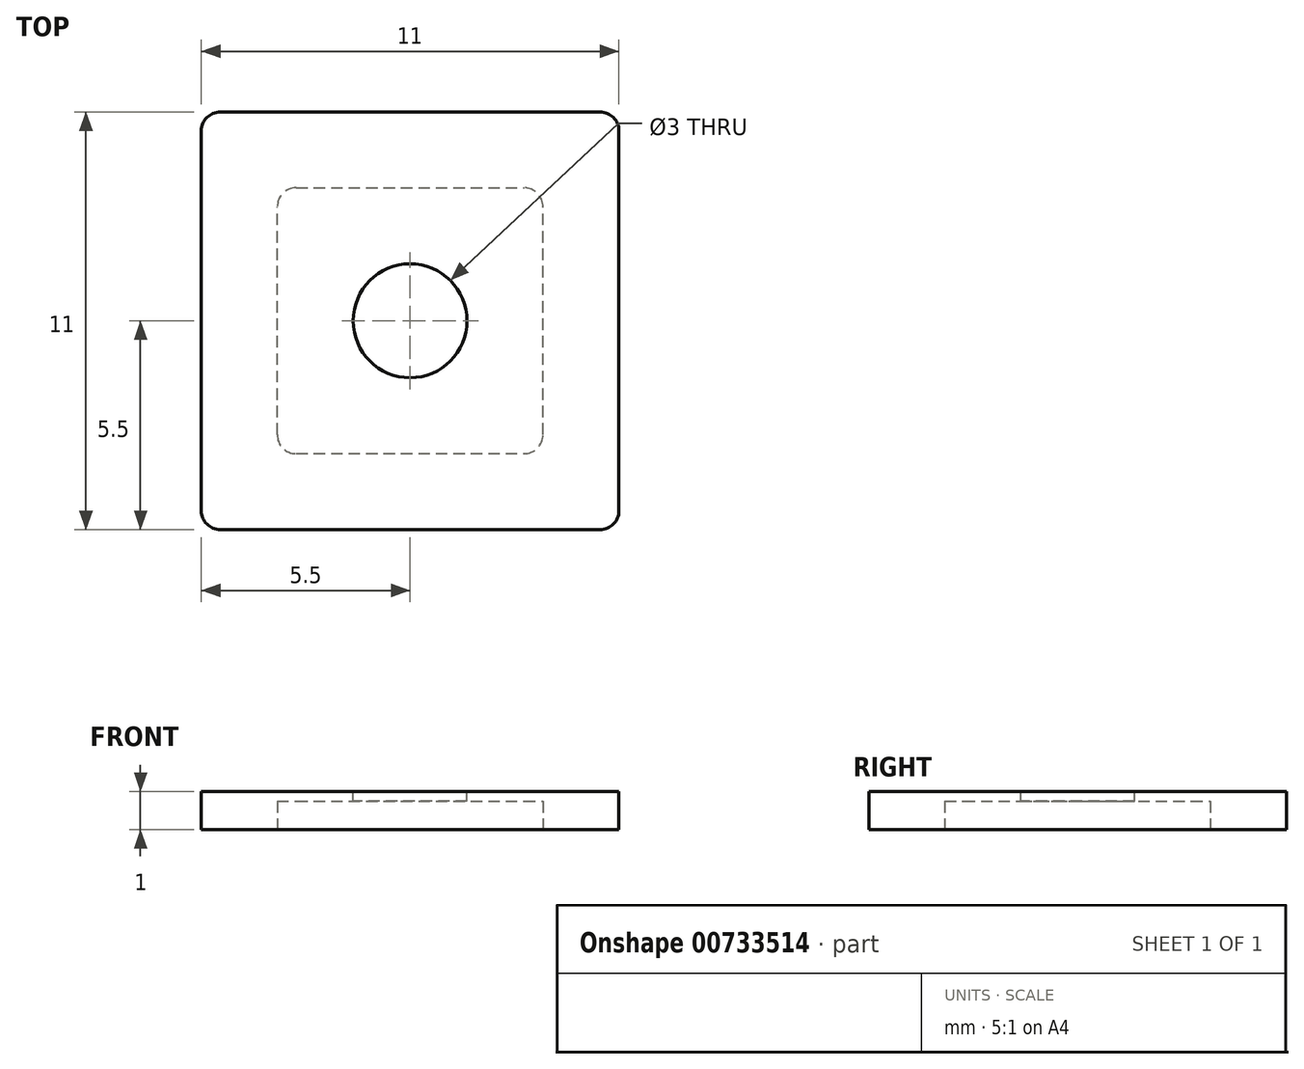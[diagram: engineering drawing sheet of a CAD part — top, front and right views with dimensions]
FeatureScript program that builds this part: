
annotation { "Feature Type Name" : "Feature", "Feature Type Description" : "" }
export const myFeature = defineFeature(function(context is Context, id is Id, definition is map)
    precondition{}
    {
        {
            var Q0;
            Q0=qCreatedBy(makeId("Top.planeOp"),FACE);
            var sketch = newSketch(context, id + "F0", { "sketchPlane" : qUnion([Q0])});
            skLineSegment(sketch, "E0.bottom", {"start": v(0, 0) * mm, "end": v(7, 0) * mm});
            skLineSegment(sketch, "E0.top", {"start": v(0, 7) * mm, "end": v(7, 7) * mm});
            skLineSegment(sketch, "E0.left", {"start": v(0, 0) * mm, "end": v(0, 7) * mm});
            skLineSegment(sketch, "E0.right", {"start": v(7, 0) * mm, "end": v(7, 7) * mm});
            skLineSegment(sketch, "E1.0", {"start": v(-2, 9) * mm, "end": v(9, 9) * mm});
            skLineSegment(sketch, "E1.1", {"start": v(-2, -2) * mm, "end": v(-2, 9) * mm});
            skLineSegment(sketch, "E1.2", {"start": v(-2, -2) * mm, "end": v(9, -2) * mm});
            skLineSegment(sketch, "E1.3", {"start": v(9, -2) * mm, "end": v(9, 9) * mm});
            skSolve(sketch);
        }
        {
            var Q0;
            Q0=makeQuery(id+"F0.imprint","IMPRINT",FACE,{"disambiguationData":[TD([[makeQuery(id+"F0.imprint","IMPRINT",EDGE,{"derivedFrom":sQuery(id+"F0.wireOp",EDGE,"E0.bottom")}),-1.0]])]});
            extrude(context, id + "F1", {"entities" : qUnion([Q0]), "depth" : 0.75 * mm, "offsetDistance" : 25 * mm});
        }
        {
            var Q0;
            Q0=makeQuery(id+"F1.opExtrude","SWEPT_EDGE",EDGE,{"disambiguationData":[OSD([sQuery(id+"F0.wireOp",EDGE,"E0.top"),sQuery(id+"F0.wireOp",EDGE,"E0.left")])]});
            var Q1;
            Q1=makeQuery(id+"F1.opExtrude","SWEPT_EDGE",EDGE,{"disambiguationData":[OSD([sQuery(id+"F0.wireOp",EDGE,"E0.top"),sQuery(id+"F0.wireOp",EDGE,"E0.right")])]});
            var Q2;
            Q2=makeQuery(id+"F1.opExtrude","SWEPT_EDGE",EDGE,{"disambiguationData":[OSD([sQuery(id+"F0.wireOp",EDGE,"E1.0"),sQuery(id+"F0.wireOp",EDGE,"E1.3")])]});
            var Q3;
            Q3=makeQuery(id+"F1.opExtrude","SWEPT_EDGE",EDGE,{"disambiguationData":[OSD([sQuery(id+"F0.wireOp",EDGE,"E1.0"),sQuery(id+"F0.wireOp",EDGE,"E1.1")])]});
            var Q4;
            Q4=makeQuery(id+"F1.opExtrude","SWEPT_EDGE",EDGE,{"disambiguationData":[OSD([sQuery(id+"F0.wireOp",EDGE,"E1.1"),sQuery(id+"F0.wireOp",EDGE,"E1.2")])]});
            var Q5;
            Q5=makeQuery(id+"F1.opExtrude","SWEPT_EDGE",EDGE,{"disambiguationData":[OSD([sQuery(id+"F0.wireOp",EDGE,"E1.2"),sQuery(id+"F0.wireOp",EDGE,"E1.3")])]});
            var Q6;
            Q6=makeQuery(id+"F1.opExtrude","SWEPT_EDGE",EDGE,{"disambiguationData":[OSD([sQuery(id+"F0.wireOp",EDGE,"E0.bottom"),sQuery(id+"F0.wireOp",EDGE,"E0.left")])]});
            var Q7;
            Q7=makeQuery(id+"F1.opExtrude","SWEPT_EDGE",EDGE,{"disambiguationData":[OSD([sQuery(id+"F0.wireOp",EDGE,"E0.bottom"),sQuery(id+"F0.wireOp",EDGE,"E0.right")])]});
            fillet(context, id + "F2", {"entities" : qUnion([Q0, Q1, Q2, Q3, Q4, Q5, Q6, Q7]), "radius" : 0.5 * mm, "tangentPropagation" : true, "allowEdgeOverflow" : false});
        }
        {
            var Q0;
            Q0=makeQuery(id+"F1.opExtrude","CAP_FACE",FACE,{"disambiguationData":[OSD([sQuery(id+"F0.wireOp",EDGE,"E0.bottom"),sQuery(id+"F0.wireOp",EDGE,"E0.top"),sQuery(id+"F0.wireOp",EDGE,"E0.left"),sQuery(id+"F0.wireOp",EDGE,"E0.right"),sQuery(id+"F0.wireOp",EDGE,"E1.0"),sQuery(id+"F0.wireOp",EDGE,"E1.1"),sQuery(id+"F0.wireOp",EDGE,"E1.2"),sQuery(id+"F0.wireOp",EDGE,"E1.3")])],"isStart":false});
            var sketch = newSketch(context, id + "F3", { "sketchPlane" : qUnion([Q0])});
            skLineSegment(sketch, "E2.0.0", {"start": v(-1.5, -2) * mm, "end": v(8.5, -2) * mm});
            skArc(sketch, "E2.0.1", {"start": v(8.5, -2) * mm, "mid": v(8.85, -1.85) * mm, "end": v(9, -1.5) * mm});
            skLineSegment(sketch, "E2.0.2", {"start": v(9, -1.5) * mm, "end": v(9, 8.5) * mm});
            skArc(sketch, "E2.0.3", {"start": v(9, 8.5) * mm, "mid": v(8.85, 8.85) * mm, "end": v(8.5, 9) * mm});
            skLineSegment(sketch, "E2.0.4", {"start": v(8.5, 9) * mm, "end": v(-1.5, 9) * mm});
            skArc(sketch, "E2.0.5", {"start": v(-1.5, 9) * mm, "mid": v(-1.85, 8.85) * mm, "end": v(-2, 8.5) * mm});
            skLineSegment(sketch, "E2.0.6", {"start": v(-2, 8.5) * mm, "end": v(-2, -1.5) * mm});
            skArc(sketch, "E2.0.7", {"start": v(-2, -1.5) * mm, "mid": v(-1.85, -1.85) * mm, "end": v(-1.5, -2) * mm});
            skSolve(sketch);
        }
        {
            var Q0;
            Q0=makeQuery(id+"F3.imprint","IMPRINT",FACE,{"disambiguationData":[TD([[makeQuery(id+"F3.imprint","IMPRINT",EDGE,{"derivedFrom":sQuery(id+"F3.wireOp",EDGE,"E2.0.0")}),1.0]])]});
            var Q1;
            {var subQ3=sQuery(id+"F0.wireOp",EDGE,"E0.bottom");Q1=makeQuery(id+"F3.imprint","IMPRINT",FACE,{"disambiguationData":[TD([[makeQuery(id+"F3.imprint","IMPRINT",EDGE,{"derivedFrom":makeQuery(id+"F1.opExtrude","CAP_EDGE",EDGE,{"disambiguationData":[OSD([subQ3])],"isStart":false})}),1.0]])]});}
            extrude(context, id + "F4", {"entities" : qUnion([Q0, Q1]), "operationType" : NewBodyOperationType.ADD, "depth" : 0.25 * mm, "offsetDistance" : 25 * mm});
        }
        {
            var Q0;
            Q0=makeQuery(id+"F4.opExtrude","CAP_FACE",FACE,{"disambiguationData":[OSD([sQuery(id+"F3.wireOp",EDGE,"E2.0.0"),sQuery(id+"F3.wireOp",EDGE,"E2.0.1"),sQuery(id+"F3.wireOp",EDGE,"E2.0.2"),sQuery(id+"F3.wireOp",EDGE,"E2.0.3"),sQuery(id+"F3.wireOp",EDGE,"E2.0.4"),sQuery(id+"F3.wireOp",EDGE,"E2.0.5"),sQuery(id+"F3.wireOp",EDGE,"E2.0.6"),sQuery(id+"F3.wireOp",EDGE,"E2.0.7")])],"isStart":false});
            var sketch = newSketch(context, id + "F5", { "sketchPlane" : qUnion([Q0])});
            skCircle(sketch, "E3", {"center": v(3.5, 3.5) * mm, "radius": 1.5 * mm});
            skPoint(sketch, "E3.centerSnap0", {"position": v(3.5, 9) * mm});
            skPoint(sketch, "E3.centerSnap1", {"position": v(-2, 3.5) * mm});
            skSolve(sketch);
        }
        {
            var Q0;
            Q0=makeQuery(id+"F5.imprint","IMPRINT",FACE,{"disambiguationData":[TD([[makeQuery(id+"F5.imprint","IMPRINT",EDGE,{"derivedFrom":sQuery(id+"F5.wireOp",EDGE,"E3")}),1.0]])]});
            extrude(context, id + "F6", {"entities" : qUnion([Q0]), "operationType" : NewBodyOperationType.REMOVE, "endBound" : BoundingType.THROUGH_ALL, "oppositeDirection" : true, "depth" : 25 * mm, "offsetDistance" : 25 * mm});
        }
    });
